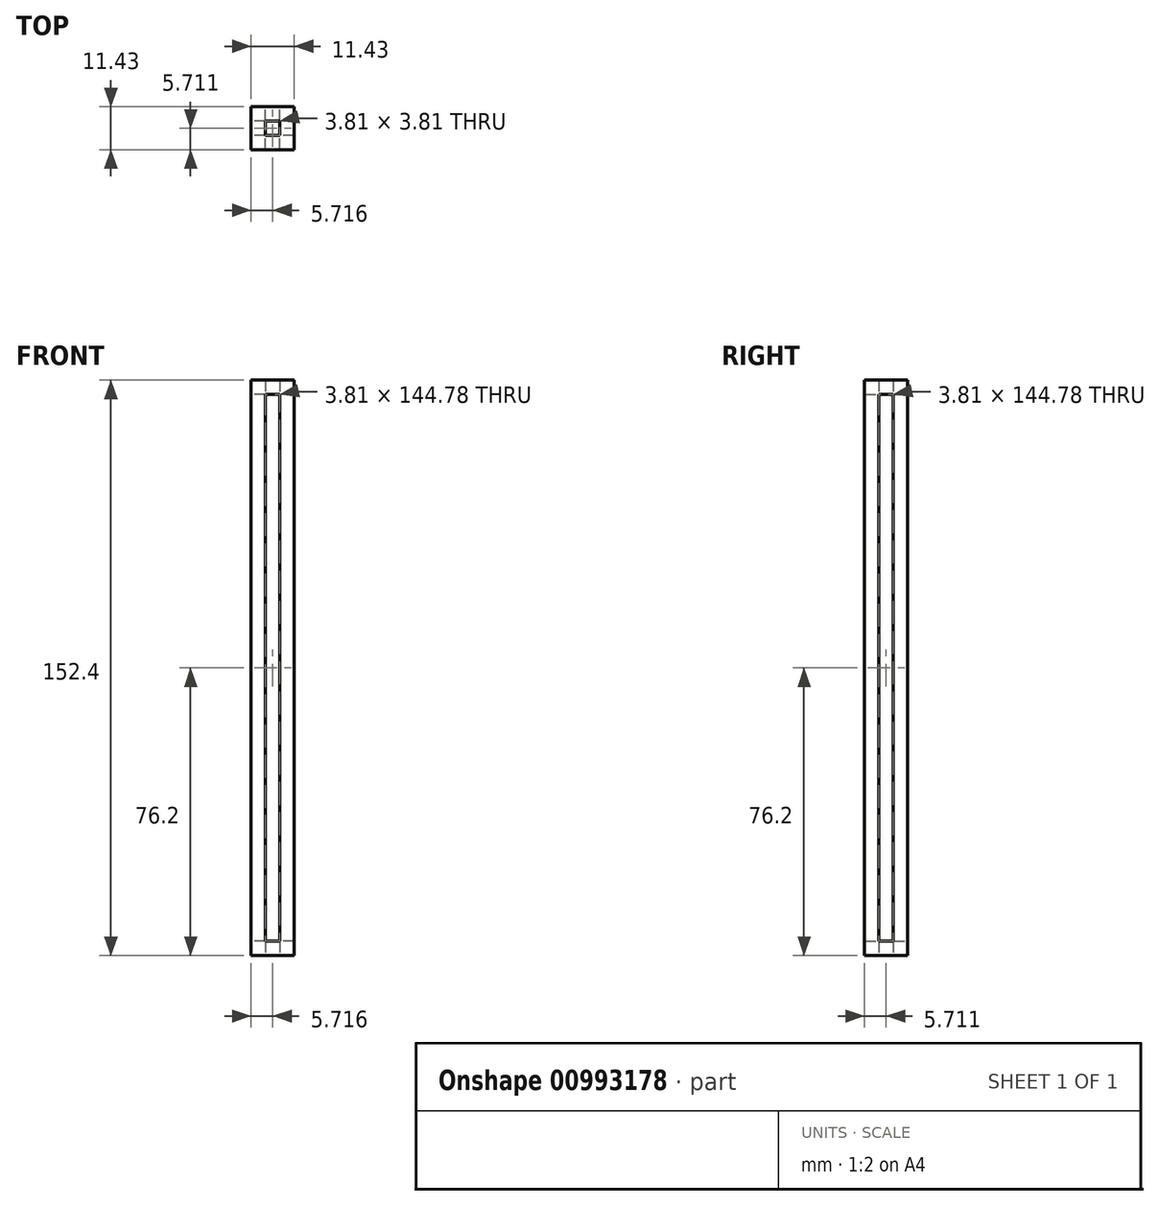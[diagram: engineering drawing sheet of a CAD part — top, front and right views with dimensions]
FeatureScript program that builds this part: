
annotation { "Feature Type Name" : "Feature", "Feature Type Description" : "" }
export const myFeature = defineFeature(function(context is Context, id is Id, definition is map)
    precondition{}
    {
        {
            var Q0;
            Q0=qCreatedBy(makeId("Top.planeOp"),FACE);
            var sketch = newSketch(context, id + "F0", { "sketchPlane" : qUnion([Q0])});
            skLineSegment(sketch, "E0.bottom", {"start": v(-60.04, -17.88) * mm, "end": v(-48.6, -17.88) * mm});
            skLineSegment(sketch, "E0.top", {"start": v(-60.04, -29.31) * mm, "end": v(-48.6, -29.31) * mm});
            skLineSegment(sketch, "E0.left", {"start": v(-60.04, -17.88) * mm, "end": v(-60.04, -29.31) * mm});
            skLineSegment(sketch, "E0.right", {"start": v(-48.6, -17.88) * mm, "end": v(-48.6, -29.31) * mm});
            skLineSegment(sketch, "E1.bottom", {"start": v(-52.42, -21.7) * mm, "end": v(-56.23, -21.7) * mm});
            skLineSegment(sketch, "E1.top", {"start": v(-52.42, -25.5) * mm, "end": v(-56.23, -25.5) * mm});
            skLineSegment(sketch, "E1.left", {"start": v(-52.42, -21.7) * mm, "end": v(-52.42, -25.5) * mm});
            skLineSegment(sketch, "E1.right", {"start": v(-56.23, -21.7) * mm, "end": v(-56.23, -25.5) * mm});
            skPoint(sketch, "E1.middle", {"position": v(-54.32, -23.6) * mm});
            skPoint(sketch, "E1.middle.positionSnap0", {"position": v(-54.32, -17.88) * mm});
            skPoint(sketch, "E1.centerSnap0", {"position": v(-54.32, -17.88) * mm});
            skSolve(sketch);
        }
        {
            var Q0;
            Q0=makeQuery(id+"F0.imprint","IMPRINT",FACE,{"disambiguationData":[TD([[makeQuery(id+"F0.imprint","IMPRINT",EDGE,{"derivedFrom":sQuery(id+"F0.wireOp",EDGE,"E0.bottom")}),-1.0]])]});
            extrude(context, id + "F1", {"entities" : qUnion([Q0]), "depth" : 152.4 * mm, "offsetDistance" : 25.4 * mm});
        }
        {
            var Q0;
            Q0=makeQuery(id+"F1.opExtrude","SWEPT_FACE",FACE,{"disambiguationData":[OSD([sQuery(id+"F0.wireOp",EDGE,"E0.left")])]});
            var sketch = newSketch(context, id + "F2", { "sketchPlane" : qUnion([Q0])});
            skLineSegment(sketch, "E2.bottom", {"start": v(21.7, 148.6) * mm, "end": v(25.5, 148.6) * mm});
            skLineSegment(sketch, "E2.top", {"start": v(21.7, 3.8) * mm, "end": v(25.5, 3.8) * mm});
            skLineSegment(sketch, "E2.left", {"start": v(21.7, 148.6) * mm, "end": v(21.7, 3.8) * mm});
            skLineSegment(sketch, "E2.right", {"start": v(25.5, 148.6) * mm, "end": v(25.5, 3.8) * mm});
            skSolve(sketch);
        }
        {
            var Q0;
            Q0=makeQuery(id+"F2.imprint","IMPRINT",FACE,{"disambiguationData":[TD([[makeQuery(id+"F2.imprint","IMPRINT",EDGE,{"derivedFrom":sQuery(id+"F2.wireOp",EDGE,"E2.bottom")}),-1.0]])]});
            extrude(context, id + "F3", {"entities" : qUnion([Q0]), "operationType" : NewBodyOperationType.REMOVE, "oppositeDirection" : true, "depth" : 25.4 * mm, "offsetDistance" : 25.4 * mm});
        }
        {
            var Q0;
            Q0=makeQuery(id+"F1.opExtrude","SWEPT_FACE",FACE,{"disambiguationData":[OSD([sQuery(id+"F0.wireOp",EDGE,"E0.bottom")])]});
            var sketch = newSketch(context, id + "F4", { "sketchPlane" : qUnion([Q0])});
            skLineSegment(sketch, "E3.bottom", {"start": v(52.42, 3.8) * mm, "end": v(56.23, 3.8) * mm});
            skLineSegment(sketch, "E3.top", {"start": v(52.42, 148.6) * mm, "end": v(56.23, 148.6) * mm});
            skLineSegment(sketch, "E3.left", {"start": v(52.42, 3.8) * mm, "end": v(52.42, 148.6) * mm});
            skLineSegment(sketch, "E3.right", {"start": v(56.23, 3.8) * mm, "end": v(56.23, 148.6) * mm});
            skSolve(sketch);
        }
        {
            var Q0;
            Q0=makeQuery(id+"F4.imprint","IMPRINT",FACE,{"disambiguationData":[TD([[makeQuery(id+"F4.imprint","IMPRINT",EDGE,{"derivedFrom":sQuery(id+"F4.wireOp",EDGE,"E3.bottom")}),1.0]])]});
            extrude(context, id + "F5", {"entities" : qUnion([Q0]), "operationType" : NewBodyOperationType.REMOVE, "oppositeDirection" : true, "depth" : 25.4 * mm, "offsetDistance" : 25.4 * mm});
        }
    });
